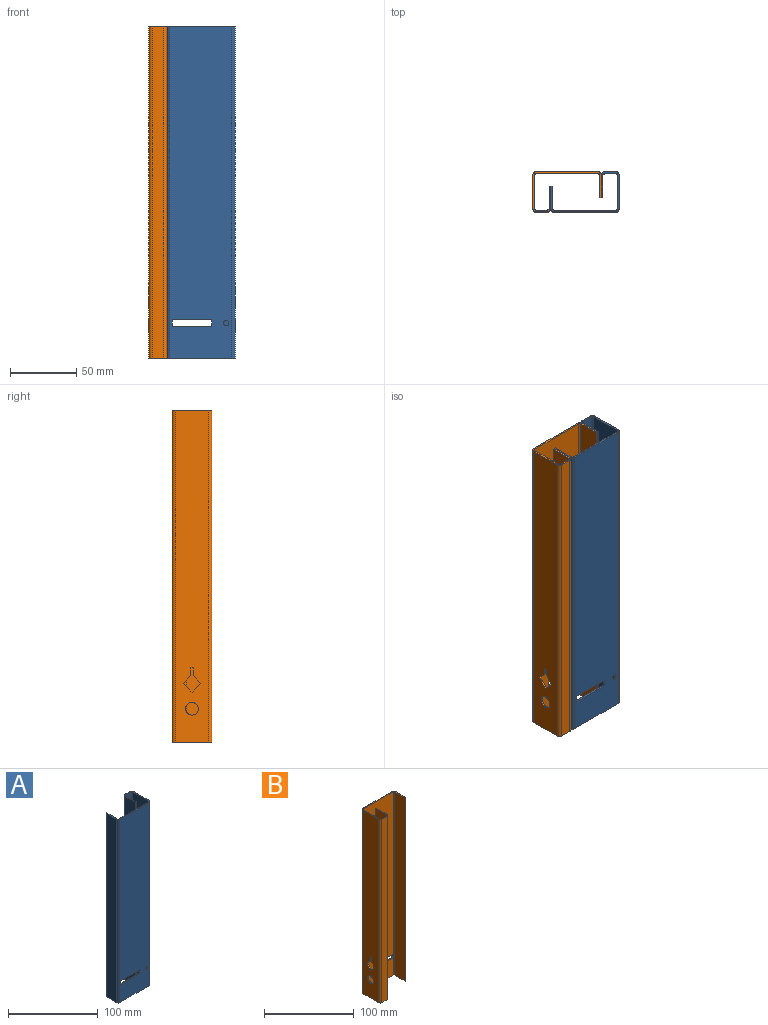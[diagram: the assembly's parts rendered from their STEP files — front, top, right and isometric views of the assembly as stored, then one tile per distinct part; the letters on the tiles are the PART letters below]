
ASSEMBLY  parts=2 mates=1
PART A: 35 faces, bbox 51.5x30x250 mm
  f0: plane 250x46.7mm, normal (0,-1,0), area 11511.1mm2, adj f2,f19,f20,f21,f22,f23,f24,f25
  f1: plane 250x46.7mm, normal (0,1,0), area 11511.1mm2, adj f14,f15,f20,f21,f22,f23,f24,f25
  f2: cylinder r=2.4mm len=250mm, axis (0,0,-1), area 942.5mm2, adj f0,f3,f20,f21
  f3: plane 250x25.2mm, normal (1,0,0), area 6128.3mm2, adj f2,f4,f20,f21,f27,f28,f29,f30
  f4: cylinder r=2.4mm len=250mm, axis (0,0,-1), area 942.5mm2, adj f3,f5,f20,f21
  f5: plane 250x8.7mm, normal (0,1,0), area 2175mm2, adj f4,f6,f20,f21
  f6: cylinder r=2.4mm len=250mm, axis (0,0,-1), area 942.5mm2, adj f5,f7,f20,f21
  f7: plane 250x16.6mm, normal (-1,0,0), area 4150mm2, adj f6,f8,f20,f21
  f8: plane 250x1.2mm, normal (0,-1,0), area 300mm2, adj f7,f9,f20,f21
  f9: plane 250x16.6mm, normal (1,0,0), area 4150mm2, adj f8,f10,f20,f21
  f10: cylinder r=1.2mm len=250mm, axis (0,0,-1), area 471.2mm2, adj f9,f11,f20,f21
  f11: plane 250x8.7mm, normal (0,-1,0), area 2175mm2, adj f10,f12,f20,f21
  f12: cylinder r=1.2mm len=250mm, axis (0,0,-1), area 471.2mm2, adj f11,f13,f20,f21
  f13: plane 250x25.2mm, normal (-1,0,0), area 6128.3mm2, adj f12,f14,f20,f21,f27,f28,f29,f30
  f14: cylinder r=1.2mm len=250mm, axis (0,0,-1), area 471.2mm2, adj f1,f13,f20,f21
  f15: cylinder r=1.2mm len=250mm, axis (0,0,-1), area 471.2mm2, adj f1,f16,f20,f21
  f16: plane 250x16.6mm, normal (1,0,0), area 4150mm2, adj f15,f17,f20,f21
  f17: plane 250x1.2mm, normal (0,1,0), area 300mm2, adj f16,f18,f20,f21
  f18: plane 250x16.6mm, normal (-1,0,0), area 4150mm2, adj f17,f19,f20,f21
  f19: cylinder r=2.4mm len=250mm, axis (0,0,-1), area 942.5mm2, adj f0,f18,f20,f21
  f20: plane 51.5x30mm, normal (0,0,1), area 150.1mm2, adj f0,f1,f2,f3,f4,f5,f6,f7
  f21: plane 51.5x30mm, normal (0,0,-1), area 150.1mm2, adj f0,f1,f2,f3,f4,f5,f6,f7
  f22: plane 5x1.2mm, normal (1,0,0), area 6mm2, adj f0,f1,f23,f25
  f23: plane 30x1.2mm, normal (0,0,1), area 36mm2, adj f0,f1,f22,f24
  f24: plane 5x1.2mm, normal (-1,0,0), area 6mm2, adj f0,f1,f23,f25
  f25: plane 30x1.2mm, normal (0,0,-1), area 36mm2, adj f0,f1,f22,f24
  f26: cylinder r=2.1mm len=4.2mm, axis (0,-1,0), area 15.8mm2, adj f0,f1
  f27: cylinder r=4.75mm len=9.5mm, axis (1,0,0), area 35.8mm2, adj f3,f13
  f28: plane 6.7x6.7mm, normal (0,0.71,0.71), area 11.4mm2, adj f3,f13,f29,f34
  f29: plane 6.7x6.7mm, normal (0,-0.71,0.71), area 11.4mm2, adj f3,f13,f28,f30
  f30: plane 5.7x5.7mm, normal (0,-0.71,-0.71), area 9.7mm2, adj f3,f13,f29,f31
  f31: plane 6x1.2mm, normal (0,-1,0), area 7.2mm2, adj f3,f13,f30,f32
  f32: plane 2x1.2mm, normal (0,0,-1), area 2.4mm2, adj f3,f13,f31,f33
  f33: plane 6x1.2mm, normal (0,1,0), area 7.2mm2, adj f3,f13,f32,f34
  f34: plane 5.7x5.7mm, normal (0,0.71,-0.71), area 9.7mm2, adj f3,f13,f28,f33
PART B: 35 faces, bbox 51.5x30x250 mm
  f0: plane 250x25.2mm, normal (-1,0,0), area 6128.3mm2, adj f4,f5,f20,f21,f27,f28,f29,f30
  f1: plane 250x25.2mm, normal (1,0,0), area 6128.3mm2, adj f13,f14,f20,f21,f27,f28,f29,f30
  f2: plane 250x46.7mm, normal (0,1,0), area 11511.1mm2, adj f4,f19,f20,f21,f22,f23,f24,f25
  f3: plane 250x46.7mm, normal (0,-1,0), area 11511.1mm2, adj f14,f15,f20,f21,f22,f23,f24,f25
  f4: cylinder r=2.4mm len=250mm, axis (0,0,-1), area 942.5mm2, adj f0,f2,f20,f21
  f5: cylinder r=2.4mm len=250mm, axis (0,0,-1), area 942.5mm2, adj f0,f6,f20,f21
  f6: plane 250x8.7mm, normal (0,-1,0), area 2175mm2, adj f5,f7,f20,f21
  f7: cylinder r=2.4mm len=250mm, axis (0,0,-1), area 942.5mm2, adj f6,f8,f20,f21
  f8: plane 250x16.6mm, normal (1,0,0), area 4150mm2, adj f7,f9,f20,f21
  f9: plane 250x1.2mm, normal (0,1,0), area 300mm2, adj f8,f10,f20,f21
  f10: plane 250x16.6mm, normal (-1,0,0), area 4150mm2, adj f9,f11,f20,f21
  f11: cylinder r=1.2mm len=250mm, axis (0,0,-1), area 471.2mm2, adj f10,f12,f20,f21
  f12: plane 250x8.7mm, normal (0,1,0), area 2175mm2, adj f11,f13,f20,f21
  f13: cylinder r=1.2mm len=250mm, axis (0,0,-1), area 471.2mm2, adj f1,f12,f20,f21
  f14: cylinder r=1.2mm len=250mm, axis (0,0,-1), area 471.2mm2, adj f1,f3,f20,f21
  f15: cylinder r=1.2mm len=250mm, axis (0,0,-1), area 471.2mm2, adj f3,f16,f20,f21
  f16: plane 250x16.6mm, normal (-1,0,0), area 4150mm2, adj f15,f17,f20,f21
  f17: plane 250x1.2mm, normal (0,-1,0), area 300mm2, adj f16,f18,f20,f21
  f18: plane 250x16.6mm, normal (1,0,0), area 4150mm2, adj f17,f19,f20,f21
  f19: cylinder r=2.4mm len=250mm, axis (0,0,-1), area 942.5mm2, adj f2,f18,f20,f21
  f20: plane 51.5x30mm, normal (0,0,1), area 150.1mm2, adj f0,f1,f2,f3,f4,f5,f6,f7
  f21: plane 51.5x30mm, normal (0,0,-1), area 150.1mm2, adj f0,f1,f2,f3,f4,f5,f6,f7
  f22: plane 5x1.2mm, normal (-1,0,0), area 6mm2, adj f2,f3,f23,f25
  f23: plane 30x1.2mm, normal (0,0,1), area 36mm2, adj f2,f3,f22,f24
  f24: plane 5x1.2mm, normal (1,0,0), area 6mm2, adj f2,f3,f23,f25
  f25: plane 30x1.2mm, normal (0,0,-1), area 36mm2, adj f2,f3,f22,f24
  f26: cylinder r=2.1mm len=4.2mm, axis (0,1,0), area 15.8mm2, adj f2,f3
  f27: cylinder r=4.75mm len=9.5mm, axis (-1,0,0), area 35.8mm2, adj f0,f1
  f28: plane 6.7x6.7mm, normal (0,0.71,0.71), area 11.4mm2, adj f0,f1,f29,f34
  f29: plane 5.7x5.7mm, normal (0,0.71,-0.71), area 9.7mm2, adj f0,f1,f28,f30
  f30: plane 6x1.2mm, normal (0,1,0), area 7.2mm2, adj f0,f1,f29,f31
  f31: plane 2x1.2mm, normal (0,0,-1), area 2.4mm2, adj f0,f1,f30,f32
  f32: plane 6x1.2mm, normal (0,-1,0), area 7.2mm2, adj f0,f1,f31,f33
  f33: plane 5.7x5.7mm, normal (0,-0.71,-0.71), area 9.7mm2, adj f0,f1,f32,f34
  f34: plane 6.7x6.7mm, normal (0,-0.71,0.71), area 11.4mm2, adj f0,f1,f28,f33
PLACE A t=(34.62,30.23,-14.92)mm
PLACE B t=(34.62,30.23,-14.92)mm
MATE fastened B.f8 <-> A.f18  axis (1,0,0) through (15.62,34.23,110.08)mm
